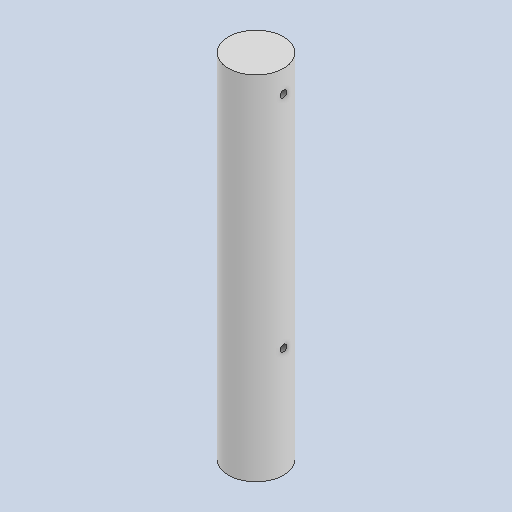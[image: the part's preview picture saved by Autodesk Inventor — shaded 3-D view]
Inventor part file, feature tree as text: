
AUTODESK INVENTOR PART (.ipt)
format: ipt  version: 2023 (Build 270158000, 158)  size: 252,416 bytes
history: native  units: mm
features: extrude x2, thread x2, sketch x2, other x1, hole x1
ambient origin geometry x8: Origin, YZ Plane, XZ Plane, XY Plane, X Axis, Y Axis, Z Axis, Center Point
bodies: Body1 (feature_tree)
feature tree (8):
  other  "Твердое тело1"
  extrude  "Выдавливание1"  Depth=25.0mm
  hole  "Отверстие1"  [1 undecoded]
  extrude  "Выдавливание3"  Depth=45.0mm
  thread  "Резьба4"
  thread  "Резьба5"
  sketch  "Эскиз1"
  sketch  "Эскиз2"
note: 1 required parameter value undecoded (feature->parameter linkage not recoverable at this tier; creation-order binding heuristic only, values carry confidence <= 0.55)
